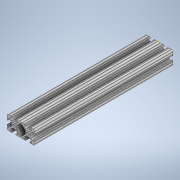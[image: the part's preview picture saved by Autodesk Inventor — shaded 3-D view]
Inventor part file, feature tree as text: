
AUTODESK INVENTOR PART (.ipt)
format: ipt  version: 2020 (Build 240168000, 168)  size: 333,312 bytes
history: native  units: in
note: dims shown in document units (in); Inventor stores cm internally (conversion verified against a paired STEP export)
features: sketch x2, extrude x1
ambient origin geometry x8: Origin, YZ Plane, XZ Plane, XY Plane, X Axis, Y Axis, Z Axis, Center Point
bodies: Solid1 (feature_tree)
feature tree (3):
  extrude  "Extrusion1"  [1 undecoded]
  sketch  "Sketch2"
  sketch  "Sketch1"  dims[d0=10.0in d1=0.0in]
note: 1 required parameter value undecoded (feature->parameter linkage not recoverable at this tier; creation-order binding heuristic only, values carry confidence <= 0.55)
